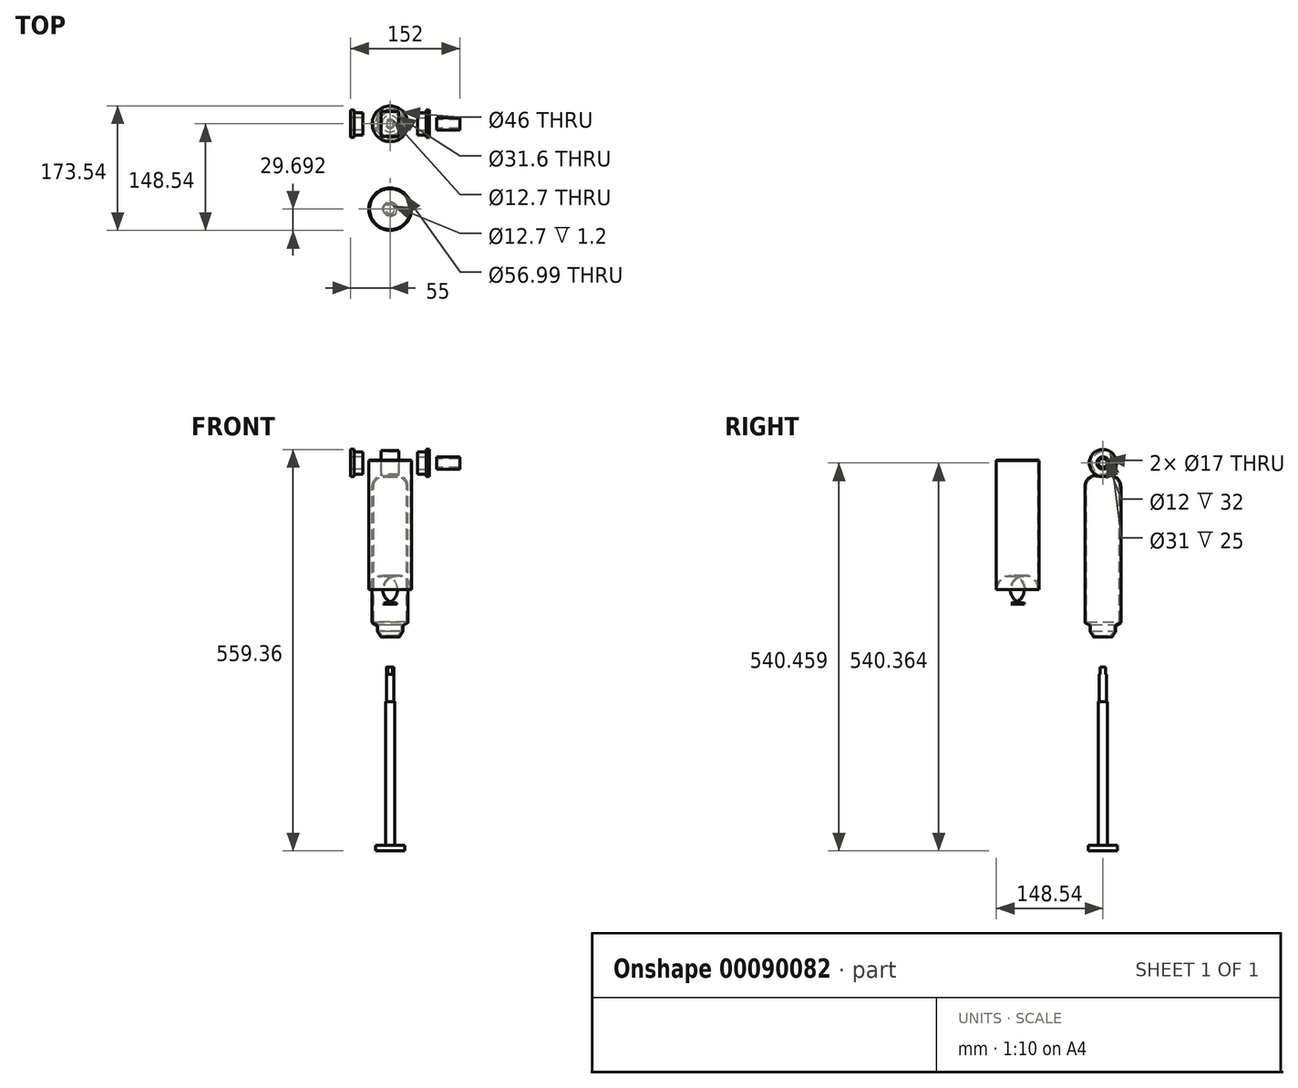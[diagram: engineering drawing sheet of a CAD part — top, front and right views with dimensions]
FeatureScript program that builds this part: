
annotation { "Feature Type Name" : "Feature", "Feature Type Description" : "" }
export const myFeature = defineFeature(function(context is Context, id is Id, definition is map)
    precondition{}
    {
        {
            var Q0;
            Q0=qCreatedBy(makeId("Right.planeOp"),FACE);
            var sketch = newSketch(context, id + "F0", { "sketchPlane" : qUnion([Q0])});
            skLineSegment(sketch, "E0", {"start": v(0, 0) * mm, "end": v(-208, 0) * mm});
            skLineSegment(sketch, "E1", {"start": v(0, 0) * mm, "end": v(0, 20.5) * mm});
            skLineSegment(sketch, "E2", {"start": v(0, 20.5) * mm, "end": v(-8, 20.5) * mm});
            skLineSegment(sketch, "E3", {"start": v(-8, 20.5) * mm, "end": v(-8, 6.35) * mm});
            skLineSegment(sketch, "E4", {"start": v(-8, 6.35) * mm, "end": v(-208, 6.35) * mm});
            skLineSegment(sketch, "E5", {"start": v(-208, 6.35) * mm, "end": v(-208, 0) * mm});
            skSolve(sketch);
        }
        {
            var Q0;
            Q0=qSketchRegion(id+"F0",true);
            var Q1;
            Q1=sQuery(id+"F0.wireOp",EDGE,"E0");
            revolve(context, id + "F1", {"entities" : qUnion([Q0]), "axis" : qUnion([Q1]), "revolveType" : RevolveType.FULL});
        }
        {
            var Q0;
            Q0=qCreatedBy(makeId("Front.planeOp"),FACE);
            var sketch = newSketch(context, id + "F2", { "sketchPlane" : qUnion([Q0])});
            skLineSegment(sketch, "E6", {"start": v(0, 0) * mm, "end": v(232.11, 0) * mm, "construction": true});
            skSolve(sketch);
        }
        {
            var Q0;
            Q0=makeQuery(id+"F1.opRevolve","SWEPT_FACE",FACE,{"disambiguationData":[OSD([sQuery(id+"F0.wireOp",EDGE,"E5")])]});
            var sketch = newSketch(context, id + "F3", { "sketchPlane" : qUnion([Q0])});
            skCircle(sketch, "E7", {"center": v(0, 0) * mm, "radius": 5 * mm});
            skSolve(sketch);
        }
        {
            var Q0;
            Q0=qSketchRegion(id+"F3",true);
            extrude(context, id + "F4", {"entities" : qUnion([Q0]), "operationType" : NewBodyOperationType.ADD, "depth" : 48 * mm});
        }
        {
            var Q0;
            Q0=makeQuery(id+"F4.opExtrude","CAP_FACE",FACE,{"disambiguationData":[OSD([sQuery(id+"F3.wireOp",EDGE,"E7")])],"isStart":false});
            var sketch = newSketch(context, id + "F5", { "sketchPlane" : qUnion([Q0])});
            skLineSegment(sketch, "E8", {"start": v(-3, 4) * mm, "end": v(3, 4) * mm});
            skLineSegment(sketch, "E9", {"start": v(-3, -4) * mm, "end": v(3, -4) * mm});
            skSolve(sketch);
        }
        {
            var Q0;
            {var subQ0=sQuery(id+"F5.wireOp",EDGE,"E8");Q0=makeQuery(id+"F5.imprint","IMPRINT",FACE,{"disambiguationData":[TD([[makeQuery(id+"F5.imprint","IMPRINT",EDGE,{"derivedFrom":subQ0}),1.0]])]});}
            var Q1;
            {var subQ0=sQuery(id+"F5.wireOp",EDGE,"E9");Q1=makeQuery(id+"F5.imprint","IMPRINT",FACE,{"disambiguationData":[TD([[makeQuery(id+"F5.imprint","IMPRINT",EDGE,{"derivedFrom":subQ0}),-1.0]])]});}
            extrude(context, id + "F6", {"entities" : qUnion([Q0, Q1]), "operationType" : NewBodyOperationType.REMOVE, "oppositeDirection" : true, "depth" : 10 * mm});
        }
        {
            var Q0;
            Q0=qCreatedBy(makeId("Right.planeOp"),FACE);
            var sketch = newSketch(context, id + "F7", { "sketchPlane" : qUnion([Q0])});
            skLineSegment(sketch, "E10", {"start": v(24.07, 0) * mm, "end": v(249.75, 0) * mm, "construction": true});
            skLineSegment(sketch, "E11", {"start": v(24.07, 0) * mm, "end": v(24.07, 10) * mm});
            skLineSegment(sketch, "E12", {"start": v(39.07, 25) * mm, "end": v(229.07, 25) * mm});
            skLineSegment(sketch, "E13", {"start": v(229.07, 25) * mm, "end": v(233.07, 17.8) * mm});
            skLineSegment(sketch, "E14", {"start": v(233.07, 17.8) * mm, "end": v(241.07, 17.8) * mm});
            skLineSegment(sketch, "E15", {"start": v(241.07, 17.8) * mm, "end": v(249.07, 12.5) * mm});
            skLineSegment(sketch, "E16", {"start": v(249.07, 12.5) * mm, "end": v(249.07, 6.35) * mm});
            skPoint(sketch, "E17.visualSharp", {"position": v(24.07, 25) * mm});
            skArc(sketch, "E17.filletArc", {"start": v(39.07, 25) * mm, "mid": v(28.46, 20.6) * mm, "end": v(24.07, 10) * mm});
            skLineSegment(sketch, "E18.1", {"start": v(39.07, 23) * mm, "end": v(227.9, 23) * mm});
            skLineSegment(sketch, "E19.0", {"start": v(247.07, 11.43) * mm, "end": v(247.07, 6.35) * mm});
            skLineSegment(sketch, "E19.1", {"start": v(240.47, 15.8) * mm, "end": v(247.07, 11.43) * mm});
            skLineSegment(sketch, "E19.2", {"start": v(231.9, 15.8) * mm, "end": v(240.47, 15.8) * mm});
            skLineSegment(sketch, "E19.3", {"start": v(227.9, 23) * mm, "end": v(231.9, 15.8) * mm});
            skLineSegment(sketch, "E20", {"start": v(247.07, 6.35) * mm, "end": v(249.07, 6.35) * mm});
            skLineSegment(sketch, "E21", {"start": v(24.07, 0) * mm, "end": v(26.07, 0) * mm});
            skLineSegment(sketch, "E22.0", {"start": v(26.07, 0) * mm, "end": v(26.07, 10) * mm});
            skArc(sketch, "E22.1", {"start": v(39.07, 23) * mm, "mid": v(29.88, 19.2) * mm, "end": v(26.07, 10) * mm});
            skSolve(sketch);
        }
        {
            var Q0;
            Q0=qSketchRegion(id+"F7",true);
            var Q1;
            Q1=sQuery(id+"F7.wireOp",EDGE,"E10");
            revolve(context, id + "F8", {"entities" : qUnion([Q0]), "axis" : qUnion([Q1]), "revolveType" : RevolveType.FULL});
        }
        {
            var Q0;
            Q0=makeQuery(id+"F8.opRevolve","SWEPT_EDGE",EDGE,{"disambiguationData":[OSD([sQuery(id+"F7.wireOp",EDGE,"E12"),sQuery(id+"F7.wireOp",EDGE,"E13")])]});
            var Q1;
            Q1=makeQuery(id+"F8.opRevolve","SWEPT_EDGE",EDGE,{"disambiguationData":[OSD([sQuery(id+"F7.wireOp",EDGE,"E14"),sQuery(id+"F7.wireOp",EDGE,"E15")])]});
            var Q2;
            Q2=makeQuery(id+"F8.opRevolve","SWEPT_EDGE",EDGE,{"disambiguationData":[OSD([sQuery(id+"F7.wireOp",EDGE,"E13"),sQuery(id+"F7.wireOp",EDGE,"E14")])]});
            var Q3;
            Q3=makeQuery(id+"F8.opRevolve","SWEPT_EDGE",EDGE,{"disambiguationData":[OSD([sQuery(id+"F7.wireOp",EDGE,"E15"),sQuery(id+"F7.wireOp",EDGE,"E16")])]});
            fillet(context, id + "F9", {"entities" : qUnion([Q0, Q1, Q2, Q3]), "radius" : 1 * mm, "tangentPropagation" : true, "allowEdgeOverflow" : false});
        }
        {
            var Q0;
            Q0=makeQuery(id+"F8.opRevolve","SWEPT_BODY",BODY,{"disambiguationData":[OSD([sQuery(id+"F7.wireOp",EDGE,"E11"),sQuery(id+"F7.wireOp",EDGE,"E12"),sQuery(id+"F7.wireOp",EDGE,"E13"),sQuery(id+"F7.wireOp",EDGE,"E14"),sQuery(id+"F7.wireOp",EDGE,"E15"),sQuery(id+"F7.wireOp",EDGE,"E16"),sQuery(id+"F7.wireOp",EDGE,"E17.filletArc"),sQuery(id+"F7.wireOp",EDGE,"E18.1"),sQuery(id+"F7.wireOp",EDGE,"E19.0"),sQuery(id+"F7.wireOp",EDGE,"E19.1"),sQuery(id+"F7.wireOp",EDGE,"E19.2"),sQuery(id+"F7.wireOp",EDGE,"E19.3"),sQuery(id+"F7.wireOp",EDGE,"E20"),sQuery(id+"F7.wireOp",EDGE,"E21"),sQuery(id+"F7.wireOp",EDGE,"E22.0"),sQuery(id+"F7.wireOp",EDGE,"E22.1")])]});
            transform(context, id + "F10", {"entities" : qUnion([Q0]), "transformType" : TransformType.TRANSLATION_3D, "dx" : 0 * mm, "dy" : -546.93 * mm, "dz" : 0 * mm, "makeCopy" : false});
        }
        {
            var Q0;
            Q0=qCreatedBy(makeId("Right.planeOp"),FACE);
            var sketch = newSketch(context, id + "F11", { "sketchPlane" : qUnion([Q0])});
            skCircle(sketch, "E23", {"center": v(-540.36, 0) * mm, "radius": 17.5 * mm});
            skCircle(sketch, "E24.0", {"center": v(-540.36, 0) * mm, "radius": 15.5 * mm});
            skSolve(sketch);
        }
        {
            var Q0;
            Q0=qSketchRegion(id+"F11",true);
            extrude(context, id + "F12", {"entities" : qUnion([Q0]), "operationType" : NewBodyOperationType.ADD, "endBound" : BoundingType.SYMMETRIC, "depth" : 25 * mm});
        }
        {
            var Q0;
            Q0=qCreatedBy(makeId("Right.planeOp"),FACE);
            cPlane(context, id + "F13", {"entities" : qUnion([Q0]), "cplaneType" : CPlaneType.OFFSET, "offset" : 50 * mm, "width" : 150 * mm, "height" : 150 * mm});
        }
        {
            var Q0;
            Q0=qCreatedBy(id+"F13.planeOp",FACE);
            var sketch = newSketch(context, id + "F14", { "sketchPlane" : qUnion([Q0])});
            skCircle(sketch, "E25", {"center": v(-540.36, 0) * mm, "radius": 15.5 * mm});
            skCircle(sketch, "E26.0", {"center": v(-540.36, 0) * mm, "radius": 8.5 * mm});
            skSolve(sketch);
        }
        {
            var Q0;
            Q0=qSketchRegion(id+"F14",true);
            extrude(context, id + "F15", {"entities" : qUnion([Q0]), "oppositeDirection" : true, "depth" : 12 * mm});
        }
        {
            var Q0;
            Q0=makeQuery(id+"F15.opExtrude","CAP_FACE",FACE,{"disambiguationData":[OSD([sQuery(id+"F14.wireOp",EDGE,"E25"),sQuery(id+"F14.wireOp",EDGE,"E26.0")])],"isStart":true});
            var sketch = newSketch(context, id + "F16", { "sketchPlane" : qUnion([Q0])});
            skCircle(sketch, "E27", {"center": v(-540.36, 0) * mm, "radius": 19 * mm});
            skCircle(sketch, "E28", {"center": v(-540.36, 0) * mm, "radius": 8.5 * mm});
            skSolve(sketch);
        }
        {
            var Q0;
            Q0=qSketchRegion(id+"F16",true);
            extrude(context, id + "F17", {"entities" : qUnion([Q0]), "operationType" : NewBodyOperationType.ADD, "depth" : 5 * mm});
        }
        {
            var Q0;
            Q0=makeQuery(id+"F15.opExtrude","SWEPT_BODY",BODY,{"disambiguationData":[OSD([sQuery(id+"F14.wireOp",EDGE,"E25"),sQuery(id+"F14.wireOp",EDGE,"E26.0")])]});
            var Q1;
            Q1=qCreatedBy(makeId("Right.planeOp"),FACE);
            mirror(context, id + "F18", {"entities" : qUnion([Q0]), "mirrorPlane" : qUnion([Q1])});
        }
        {
            var Q0;
            Q0=makeQuery(id+"F17.opExtrude","CAP_FACE",FACE,{"disambiguationData":[OSD([sQuery(id+"F16.wireOp",EDGE,"E27"),sQuery(id+"F16.wireOp",EDGE,"E28")])],"isStart":false});
            cPlane(context, id + "F19", {"entities" : qUnion([Q0]), "cplaneType" : CPlaneType.OFFSET, "offset" : 10 * mm, "width" : 150 * mm, "height" : 150 * mm});
        }
        {
            var Q0;
            Q0=qCreatedBy(id+"F19.planeOp",FACE);
            var sketch = newSketch(context, id + "F20", { "sketchPlane" : qUnion([Q0])});
            skCircle(sketch, "E29", {"center": v(-540.46, 0) * mm, "radius": 8.5 * mm});
            skCircle(sketch, "E30", {"center": v(-540.46, 0) * mm, "radius": 6 * mm});
            skSolve(sketch);
        }
        {
            var Q0;
            Q0=qSketchRegion(id+"F20",true);
            extrude(context, id + "F21", {"entities" : qUnion([Q0]), "depth" : 32 * mm});
        }
        {
            var Q0;
            Q0=qCreatedBy(makeId("Right.planeOp"),FACE);
            var sketch = newSketch(context, id + "F22", { "sketchPlane" : qUnion([Q0])});
            skLineSegment(sketch, "E31", {"start": v(-546.17, -118.85) * mm, "end": v(-317.06, -118.85) * mm, "construction": true});
            skLineSegment(sketch, "E32", {"start": v(-544.07, -89.15) * mm, "end": v(-364.07, -89.15) * mm});
            skPoint(sketch, "E33.visualSharp", {"position": v(-344.07, -89.15) * mm});
            skArc(sketch, "E33.filletArc", {"start": v(-344.07, -109.15) * mm, "mid": v(-349.93, -95) * mm, "end": v(-364.07, -89.15) * mm});
            skLineSegment(sketch, "E34.0", {"start": v(-345.27, -109.15) * mm, "end": v(-345.27, -112.5) * mm});
            skArc(sketch, "E34.1", {"start": v(-345.27, -109.15) * mm, "mid": v(-350.78, -95.86) * mm, "end": v(-364.07, -90.35) * mm});
            skLineSegment(sketch, "E34.2", {"start": v(-544.34, -90.35) * mm, "end": v(-364.07, -90.35) * mm});
            skLineSegment(sketch, "E35", {"start": v(-544.07, -89.15) * mm, "end": v(-544.34, -90.35) * mm});
            skLineSegment(sketch, "E36", {"start": v(-344.07, -109.15) * mm, "end": v(-344.07, -112.5) * mm});
            skLineSegment(sketch, "E37", {"start": v(-344.07, -112.5) * mm, "end": v(-345.27, -112.5) * mm});
            skSolve(sketch);
        }
        {
            var Q0;
            Q0=qSketchRegion(id+"F22",true);
            var Q1;
            Q1=sQuery(id+"F22.wireOp",EDGE,"E31");
            revolve(context, id + "F23", {"entities" : qUnion([Q0]), "axis" : qUnion([Q1]), "revolveType" : RevolveType.FULL});
        }
        {
            var Q0;
            Q0=makeQuery(id+"F1.opRevolve","SWEPT_BODY",BODY,{"disambiguationData":[OSD([sQuery(id+"F0.wireOp",EDGE,"E0"),sQuery(id+"F0.wireOp",EDGE,"E1"),sQuery(id+"F0.wireOp",EDGE,"E2"),sQuery(id+"F0.wireOp",EDGE,"E3"),sQuery(id+"F0.wireOp",EDGE,"E4"),sQuery(id+"F0.wireOp",EDGE,"E5")])]});
            var Q1;
            Q1=makeQuery(id+"F15.opExtrude","SWEPT_BODY",BODY,{"disambiguationData":[OSD([sQuery(id+"F14.wireOp",EDGE,"E25"),sQuery(id+"F14.wireOp",EDGE,"E26.0")])]});
            var Q2;
            Q2=makeQuery(id+"F21.opExtrude","SWEPT_BODY",BODY,{"disambiguationData":[OSD([sQuery(id+"F20.wireOp",EDGE,"E29"),sQuery(id+"F20.wireOp",EDGE,"E30")])]});
            var Q3;
            Q3=makeQuery(id+"F12.opExtrude","SWEPT_BODY",BODY,{"disambiguationData":[OSD([sQuery(id+"F11.wireOp",EDGE,"E23"),sQuery(id+"F11.wireOp",EDGE,"E24.0")])]});
            var Q4;
            Q4=makeQuery(id+"F18.opPattern","COPY",BODY,{"derivedFrom":makeQuery(id+"F15.opExtrude","SWEPT_BODY",BODY,{"disambiguationData":[OSD([sQuery(id+"F14.wireOp",EDGE,"E25"),sQuery(id+"F14.wireOp",EDGE,"E26.0")])]}),"instanceName":"1"});
            var Q5;
            Q5=makeQuery(id+"F8.opRevolve","SWEPT_BODY",BODY,{"disambiguationData":[OSD([sQuery(id+"F7.wireOp",EDGE,"E11"),sQuery(id+"F7.wireOp",EDGE,"E12"),sQuery(id+"F7.wireOp",EDGE,"E13"),sQuery(id+"F7.wireOp",EDGE,"E14"),sQuery(id+"F7.wireOp",EDGE,"E15"),sQuery(id+"F7.wireOp",EDGE,"E16"),sQuery(id+"F7.wireOp",EDGE,"E17.filletArc"),sQuery(id+"F7.wireOp",EDGE,"E18.1"),sQuery(id+"F7.wireOp",EDGE,"E19.0"),sQuery(id+"F7.wireOp",EDGE,"E19.1"),sQuery(id+"F7.wireOp",EDGE,"E19.2"),sQuery(id+"F7.wireOp",EDGE,"E19.3"),sQuery(id+"F7.wireOp",EDGE,"E20"),sQuery(id+"F7.wireOp",EDGE,"E21"),sQuery(id+"F7.wireOp",EDGE,"E22.0"),sQuery(id+"F7.wireOp",EDGE,"E22.1")])]});
            var Q6;
            Q6=makeQuery(id+"F23.opRevolve","SWEPT_BODY",BODY,{"disambiguationData":[OSD([sQuery(id+"F22.wireOp",EDGE,"E32"),sQuery(id+"F22.wireOp",EDGE,"E33.filletArc"),sQuery(id+"F22.wireOp",EDGE,"E34.0"),sQuery(id+"F22.wireOp",EDGE,"E34.1"),sQuery(id+"F22.wireOp",EDGE,"E34.2"),sQuery(id+"F22.wireOp",EDGE,"E35"),sQuery(id+"F22.wireOp",EDGE,"E36"),sQuery(id+"F22.wireOp",EDGE,"E37")])]});
            var Q7;
            Q7=sQuery(id+"F2.wireOp",EDGE,"E6");
            transform(context, id + "F24", {"entities" : qUnion([Q0, Q1, Q2, Q3, Q4, Q5, Q6]), "transformType" : TransformType.ROTATION, "transformAxis" : qUnion([Q7]), "angle" : 270 * degree, "makeCopy" : false});
        }
    });
